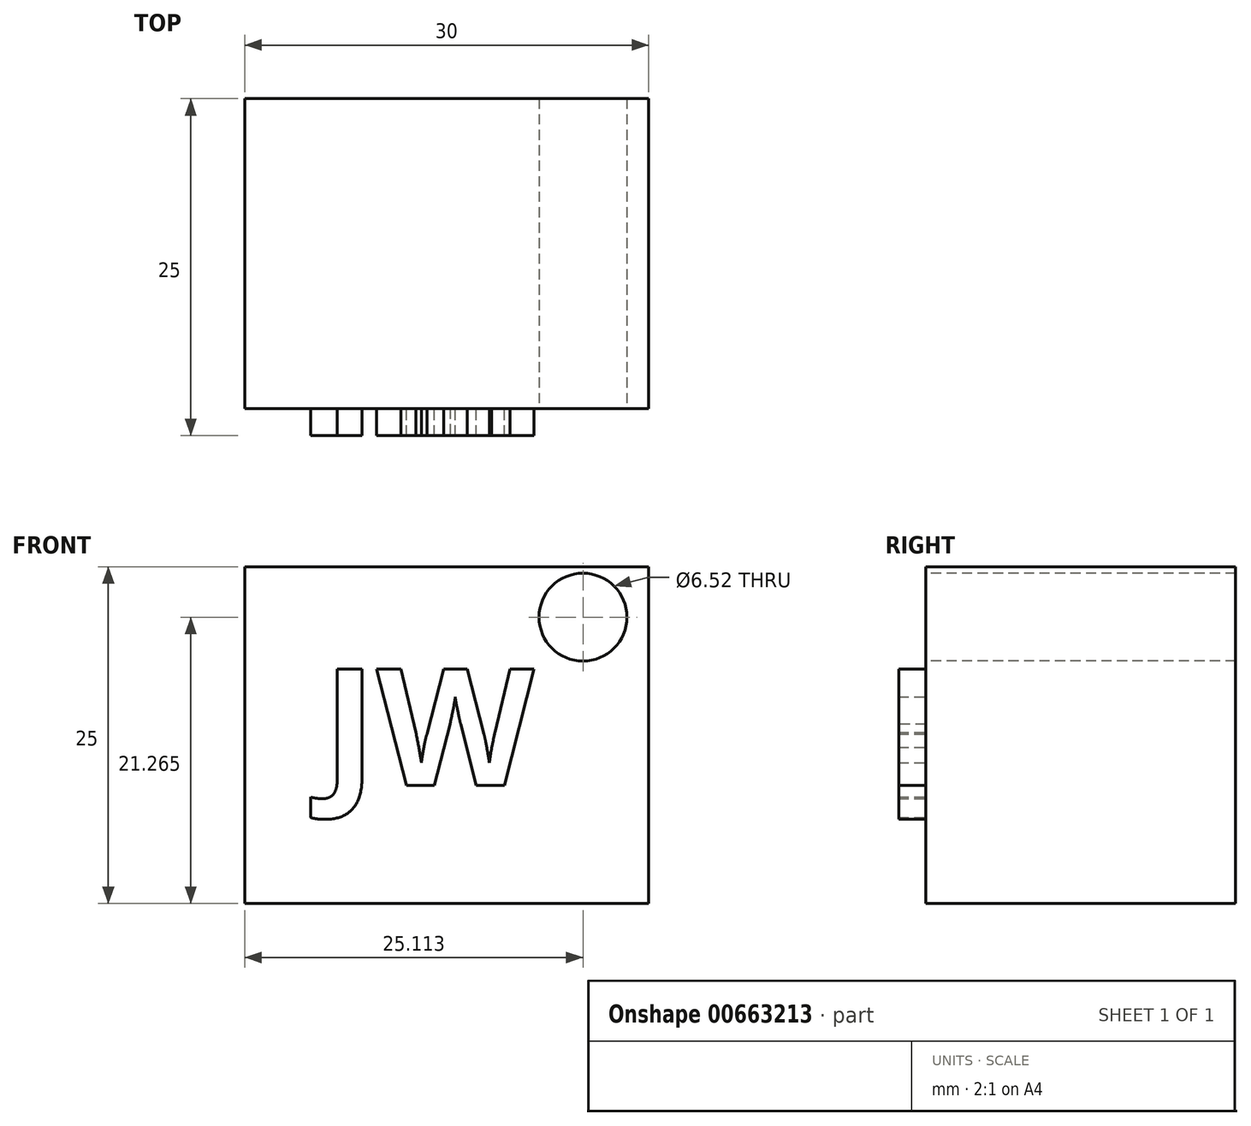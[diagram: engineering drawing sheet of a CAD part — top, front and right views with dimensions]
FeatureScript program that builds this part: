
annotation { "Feature Type Name" : "Feature", "Feature Type Description" : "" }
export const myFeature = defineFeature(function(context is Context, id is Id, definition is map)
    precondition{}
    {
        {
            var Q0;
            Q0=qCreatedBy(makeId("Front.planeOp"),FACE);
            var sketch = newSketch(context, id + "F0", { "sketchPlane" : qUnion([Q0])});
            skLineSegment(sketch, "E0.bottom", {"start": v(-15, 12.5) * mm, "end": v(15, 12.5) * mm});
            skLineSegment(sketch, "E0.top", {"start": v(-15, -12.5) * mm, "end": v(15, -12.5) * mm});
            skLineSegment(sketch, "E0.left", {"start": v(-15, 12.5) * mm, "end": v(-15, -12.5) * mm});
            skLineSegment(sketch, "E0.right", {"start": v(15, 12.5) * mm, "end": v(15, -12.5) * mm});
            skPoint(sketch, "E0.middle", {"position": v(0, 0) * mm});
            skSolve(sketch);
        }
        {
            var Q0;
            Q0=makeQuery(id+"F0.imprint","IMPRINT",FACE,{"disambiguationData":[TD([[makeQuery(id+"F0.imprint","IMPRINT",EDGE,{"derivedFrom":sQuery(id+"F0.wireOp",EDGE,"E0.bottom")}),-1.0]])]});
            var sketch = newSketch(context, id + "F1", { "sketchPlane" : qUnion([Q0])});
            skText(sketch, "E1", { "text": "JW", "fontName": "OpenSans-Bold.ttf"});
            const initialGuessF1  = {"E1": [-0.0092, -0.00371, 1, 0, 0.0087]};
            skSetInitialGuess(sketch, initialGuessF1);
            skSolve(sketch);
        }
        {
            var Q0;
            Q0=makeQuery(id+"F0.imprint","IMPRINT",FACE,{"disambiguationData":[TD([[makeQuery(id+"F0.imprint","IMPRINT",EDGE,{"derivedFrom":sQuery(id+"F0.wireOp",EDGE,"E0.bottom")}),-1.0]])]});
            extrude(context, id + "F2", {"entities" : qUnion([Q0]), "oppositeDirection" : true, "depth" : 23 * mm, "offsetDistance" : 25 * mm});
        }
        {
            var Q0;
            Q0 = qSketchRegion(id + "F1", true);
            extrude(context, id + "F3", {"entities" : qUnion([Q0]), "operationType" : NewBodyOperationType.ADD, "depth" : 2 * mm, "offsetDistance" : 25 * mm});
        }
        {
            var Q0;
            Q0=makeQuery(id+"F2.opExtrude","CAP_FACE",FACE,{"disambiguationData":[OSD([sQuery(id+"F0.wireOp",EDGE,"E0.bottom"),sQuery(id+"F0.wireOp",EDGE,"E0.top"),sQuery(id+"F0.wireOp",EDGE,"E0.left"),sQuery(id+"F0.wireOp",EDGE,"E0.right")])],"isStart":true});
            var sketch = newSketch(context, id + "F4", { "sketchPlane" : qUnion([Q0])});
            skCircle(sketch, "E2", {"center": v(10.11, 8.76) * mm, "radius": 3.26 * mm});
            skSolve(sketch);
        }
        {
            var Q0;
            Q0 = qSketchRegion(id + "F4", true);
            extrude(context, id + "F5", {"entities" : qUnion([Q0]), "operationType" : NewBodyOperationType.REMOVE, "oppositeDirection" : true, "depth" : 42.3 * mm, "offsetDistance" : 25 * mm});
        }
    });
